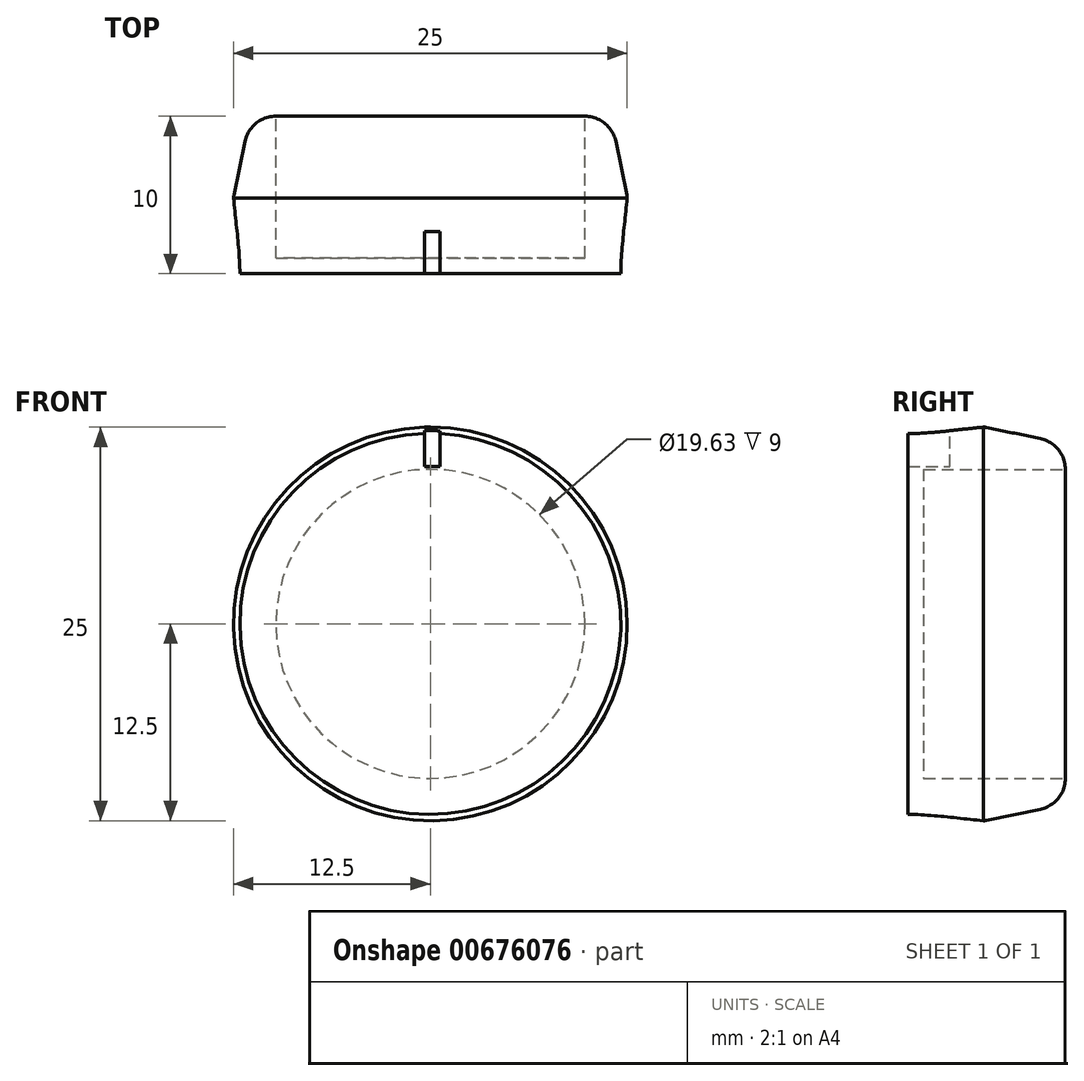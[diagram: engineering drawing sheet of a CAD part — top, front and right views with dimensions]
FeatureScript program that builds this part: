
annotation { "Feature Type Name" : "Feature", "Feature Type Description" : "" }
export const myFeature = defineFeature(function(context is Context, id is Id, definition is map)
    precondition{}
    {
        {
            var Q0;
            Q0=qCreatedBy(makeId("Top.planeOp"),FACE);
            var sketch = newSketch(context, id + "F0", { "sketchPlane" : qUnion([Q0])});
            skLineSegment(sketch, "E0.bottom", {"start": v(-3.57, 5) * mm, "end": v(6.25, 5) * mm});
            skLineSegment(sketch, "E0.top", {"start": v(-5.85, -5) * mm, "end": v(6.25, -5) * mm});
            skLineSegment(sketch, "E0.right", {"start": v(6.25, 5) * mm, "end": v(6.25, -5) * mm});
            skPoint(sketch, "E0.middle", {"position": v(0, 0) * mm});
            skLineSegment(sketch, "E1", {"start": v(-6.23, 0) * mm, "end": v(-5.52, 3.4) * mm});
            skArc(sketch, "E2.filletArc", {"start": v(-3.57, 5) * mm, "mid": v(-4.83, 4.55) * mm, "end": v(-5.52, 3.4) * mm});
            skPoint(sketch, "E3.newPointA", {"position": v(-6.25, -0.1) * mm});
            skArc(sketch, "E3.filletArc", {"start": v(-6.23, 0) * mm, "mid": v(-6.24, -0.1) * mm, "end": v(-6.25, -0.2) * mm});
            skFitSpline(sketch, "E4", {"points": [v(-6.25, -0.2) * mm, v(-5.85, -5) * mm, v(-5.8, -7.65) * mm], "startDerivative": vector(0.87, -8.97) * mm, "endDerivative": vector(1.27, -5.71) * mm});
            skSolve(sketch);
        }
        {
            var Q0;
            Q0=makeQuery(id+"F0.imprint","IMPRINT",FACE,{"disambiguationData":[TD([[makeQuery(id+"F0.imprint","IMPRINT",EDGE,{"derivedFrom":sQuery(id+"F0.wireOp",EDGE,"E0.bottom")}),-1.0]])]});
            var Q1;
            Q1=sQuery(id+"F0.wireOp",EDGE,"E0.right");
            revolve(context, id + "F1", {"entities" : qUnion([Q0]), "axis" : qUnion([Q1]), "revolveType" : RevolveType.FULL});
        }
        {
            var Q0;
            Q0=makeQuery(id+"F1.opRevolve","SWEPT_FACE",FACE,{"disambiguationData":[OSD([sQuery(id+"F0.wireOp",EDGE,"E0.bottom")])]});
            var sketch = newSketch(context, id + "F2", { "sketchPlane" : qUnion([Q0])});
            skSolve(sketch);
        }
        {
            var Q0;
            Q0=makeQuery(id+"F2.imprint","IMPRINT",FACE,{"disambiguationData":[TD([[makeQuery(id+"F2.imprint","IMPRINT",EDGE,{"derivedFrom":makeQuery(id+"F1.opRevolve","SWEPT_EDGE",EDGE,{"disambiguationData":[OSD([sQuery(id+"F0.wireOp",EDGE,"E0.bottom"),sQuery(id+"F0.wireOp",EDGE,"E2.filletArc")])]})}),1.0]])]});
            extrude(context, id + "F3", {"entities" : qUnion([Q0]), "operationType" : NewBodyOperationType.REMOVE, "oppositeDirection" : true, "depth" : 9 * mm, "offsetDistance" : 25 * mm});
        }
        {
            var Q0;
            Q0=qCreatedBy(makeId("Top.planeOp"),FACE);
            cPlane(context, id + "F4", {"entities" : qUnion([Q0]), "cplaneType" : CPlaneType.OFFSET, "offset" : 20 * mm, "width" : 150 * mm, "height" : 150 * mm});
        }
        {
            var Q0;
            Q0=qCreatedBy(id+"F4.planeOp",FACE);
            var sketch = newSketch(context, id + "F5", { "sketchPlane" : qUnion([Q0])});
            skLineSegment(sketch, "E5.bottom", {"start": v(5.88, -5.32) * mm, "end": v(6.88, -5.32) * mm});
            skLineSegment(sketch, "E5.top", {"start": v(5.88, -2.32) * mm, "end": v(6.88, -2.32) * mm});
            skLineSegment(sketch, "E5.left", {"start": v(5.88, -5.32) * mm, "end": v(5.88, -2.32) * mm});
            skLineSegment(sketch, "E5.right", {"start": v(6.88, -5.32) * mm, "end": v(6.88, -2.32) * mm});
            skSolve(sketch);
        }
        {
            var Q0;
            Q0 = qSketchRegion(id + "F5", true);
            extrude(context, id + "F6", {"entities" : qUnion([Q0]), "operationType" : NewBodyOperationType.REMOVE, "oppositeDirection" : true, "depth" : 10 * mm, "offsetDistance" : 25 * mm});
        }
    });
